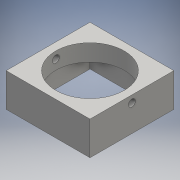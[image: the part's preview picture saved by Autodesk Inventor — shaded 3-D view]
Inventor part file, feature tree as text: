
AUTODESK INVENTOR PART (.ipt)
format: ipt  version: 2016 (Build 200138000, 138)  size: 147,968 bytes
history: native  units: mm
features: extrude x3, sketch x3, hole x1, pattern_circular x1
ambient origin geometry x8: Origin, YZ Plane, XZ Plane, XY Plane, X Axis, Y Axis, Z Axis, Center Point
bodies: Solid1 (feature_tree)
feature tree (8):
  extrude  "Extrusion1"  Depth=50.0mm
  extrude  "Extrusion2"  Depth=25.0mm
  hole  "Hole1"  [1 undecoded]
  pattern_circular  "Circular Pattern1"  [2 undecoded]
  extrude  "Extrusion3"  Depth=2.0mm TaperAngle=0.0deg
  sketch  "Sketch1"  dims[d0=50.0mm d1=50.0mm]
  sketch  "Sketch2"  dims[d2=25.0mm d3=25.0mm]
  sketch  "Sketch3"  dims[d4=5.0mm d5=12.0mm d6=0.0mm d7=49.0mm d8=12.0mm d9=0.0mm d10=4.0mm d11=4.0mm d12=8.0mm d13=6.0mm d14=4.0mm d15=2.0mm d16=90.0deg d17=5.0mm d18=20.594885mm d19=40.0mm d20=360.0deg d22=5.0mm d23=19.0mm d24=30.0mm d25=12.0mm d26=0.0mm]
note: 3 required parameter values undecoded (feature->parameter linkage not recoverable at this tier; creation-order binding heuristic only, values carry confidence <= 0.55)
